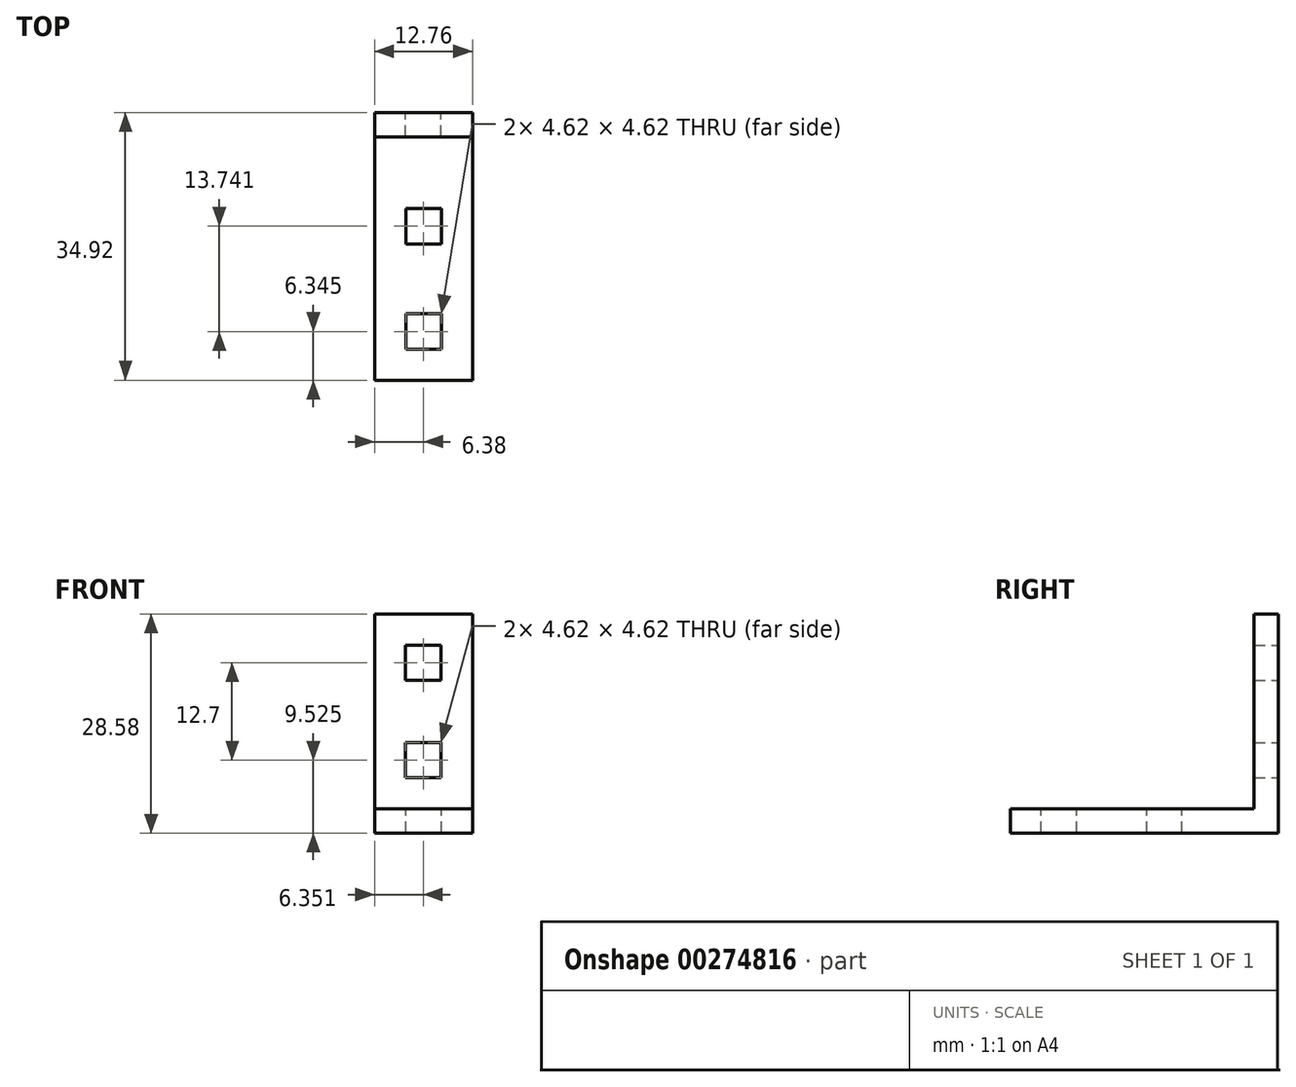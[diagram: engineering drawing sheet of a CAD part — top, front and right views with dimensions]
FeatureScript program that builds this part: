
annotation { "Feature Type Name" : "Feature", "Feature Type Description" : "" }
export const myFeature = defineFeature(function(context is Context, id is Id, definition is map)
    precondition{}
    {
        {
            var Q0;
            Q0=qCreatedBy(makeId("Front.planeOp"),FACE);
            var sketch = newSketch(context, id + "F0", { "sketchPlane" : qUnion([Q0])});
            skLineSegment(sketch, "E0.bottom", {"start": v(6.38, 15.88) * mm, "end": v(-6.38, 15.88) * mm});
            skLineSegment(sketch, "E0.left", {"start": v(6.38, 15.88) * mm, "end": v(6.38, -12.7) * mm});
            skLineSegment(sketch, "E0.right", {"start": v(-6.38, 15.88) * mm, "end": v(-6.38, -12.7) * mm});
            skPoint(sketch, "E0.middle", {"position": v(0, 0) * mm});
            skLineSegment(sketch, "E1", {"start": v(-2.34, 11.84) * mm, "end": v(2.29, 11.84) * mm});
            skLineSegment(sketch, "E2.bottom", {"start": v(-2.34, 11.84) * mm, "end": v(2.28, 11.84) * mm});
            skLineSegment(sketch, "E2.top", {"start": v(-2.34, 7.21) * mm, "end": v(2.28, 7.21) * mm});
            skLineSegment(sketch, "E2.left", {"start": v(-2.34, 11.84) * mm, "end": v(-2.34, 7.21) * mm});
            skLineSegment(sketch, "E2.right", {"start": v(2.28, 11.84) * mm, "end": v(2.28, 7.21) * mm});
            skLineSegment(sketch, "E3.MirrorCS", {"start": v(-2.34, -5.49) * mm, "end": v(2.29, -5.49) * mm});
            skLineSegment(sketch, "E4.MirrorCS", {"start": v(-2.34, -0.86) * mm, "end": v(2.28, -0.86) * mm});
            skLineSegment(sketch, "E5.MirrorCS", {"start": v(-2.34, -5.49) * mm, "end": v(2.28, -5.49) * mm});
            skLineSegment(sketch, "E6.MirrorCS", {"start": v(2.28, -5.49) * mm, "end": v(2.28, -0.86) * mm});
            skLineSegment(sketch, "E7.MirrorCS", {"start": v(-2.34, -5.49) * mm, "end": v(-2.34, -0.86) * mm});
            skLineSegment(sketch, "E8", {"start": v(2.71, -12.7) * mm, "end": v(-6.38, -12.7) * mm});
            skLineSegment(sketch, "E9", {"start": v(-6.38, -12.7) * mm, "end": v(6.38, -12.7) * mm});
            skPoint(sketch, "E0.top.start.orphan", {"position": v(6.38, -15.88) * mm});
            skPoint(sketch, "E10.orphan", {"position": v(-6.38, -15.88) * mm});
            skLineSegment(sketch, "E11", {"start": v(-1.83, -9.53) * mm, "end": v(-6.38, -9.53) * mm});
            skLineSegment(sketch, "E12", {"start": v(-6.38, -9.53) * mm, "end": v(6.38, -9.53) * mm});
            skSolve(sketch);
        }
        {
            var Q0;
            Q0=makeQuery(id+"F0.imprint","IMPRINT",FACE,{"disambiguationData":[TD([[makeQuery(id+"F0.imprint","IMPRINT",EDGE,{"derivedFrom":sQuery(id+"F0.wireOp",EDGE,"E0.bottom")}),1.0]])]});
            extrude(context, id + "F1", {"entities" : qUnion([Q0]), "depth" : 3.17 * mm});
        }
        {
            var Q0;
            {var subQ5=sQuery(id+"F0.wireOp",EDGE,"E12");var subQ8=makeQuery(id+"F0.imprint","IMPRINT",VERTEX,{"derivedFrom":subQ5});Q0=makeQuery(id+"F0.imprint","IMPRINT",FACE,{"disambiguationData":[TD([[makeQuery(id+"F0.imprint","IMPRINT",EDGE,{"disambiguationData":[TD([[subQ8,1.0]])],"derivedFrom":subQ5}),-1.0]])]});}
            extrude(context, id + "F2", {"entities" : qUnion([Q0]), "operationType" : NewBodyOperationType.ADD, "depth" : 34.92 * mm});
        }
        {
            var Q0;
            Q0=makeQuery(id+"F2.opExtrude","SWEPT_FACE",FACE,{"disambiguationData":[OSD([sQuery(id+"F0.wireOp",EDGE,"E12")])]});
            var sketch = newSketch(context, id + "F3", { "sketchPlane" : qUnion([Q0])});
            skPoint(sketch, "E13.endSnap0", {"position": v(0, -34.93) * mm});
            skLineSegment(sketch, "E14", {"start": v(0, -30.89) * mm, "end": v(2.31, -30.89) * mm});
            skLineSegment(sketch, "E15.bottom", {"start": v(2.31, -30.89) * mm, "end": v(-2.31, -30.89) * mm});
            skLineSegment(sketch, "E15.top", {"start": v(2.31, -26.26) * mm, "end": v(-2.31, -26.26) * mm});
            skLineSegment(sketch, "E15.left", {"start": v(2.31, -30.89) * mm, "end": v(2.31, -26.26) * mm});
            skLineSegment(sketch, "E15.right", {"start": v(-2.31, -30.89) * mm, "end": v(-2.31, -26.26) * mm});
            skLineSegment(sketch, "E16.bottom", {"start": v(2.31, -17.15) * mm, "end": v(-2.31, -17.15) * mm});
            skLineSegment(sketch, "E16.top", {"start": v(2.31, -12.52) * mm, "end": v(-2.31, -12.52) * mm});
            skLineSegment(sketch, "E16.left", {"start": v(2.31, -17.15) * mm, "end": v(2.31, -12.52) * mm});
            skLineSegment(sketch, "E16.right", {"start": v(-2.31, -17.15) * mm, "end": v(-2.31, -12.52) * mm});
            skSolve(sketch);
        }
        {
            var Q0;
            Q0=makeQuery(id+"F3.imprint","IMPRINT",FACE,{"disambiguationData":[TD([[makeQuery(id+"F3.imprint","IMPRINT",EDGE,{"derivedFrom":sQuery(id+"F3.wireOp",EDGE,"E16.bottom")}),-1.0]])]});
            var Q1;
            Q1=makeQuery(id+"F3.imprint","IMPRINT",FACE,{"disambiguationData":[TD([[makeQuery(id+"F3.imprint","IMPRINT",EDGE,{"derivedFrom":sQuery(id+"F3.wireOp",EDGE,"E15.top")}),1.0]])]});
            extrude(context, id + "F4", {"entities" : qUnion([Q0, Q1]), "operationType" : NewBodyOperationType.REMOVE, "oppositeDirection" : true, "depth" : 25.4 * mm});
        }
    });
